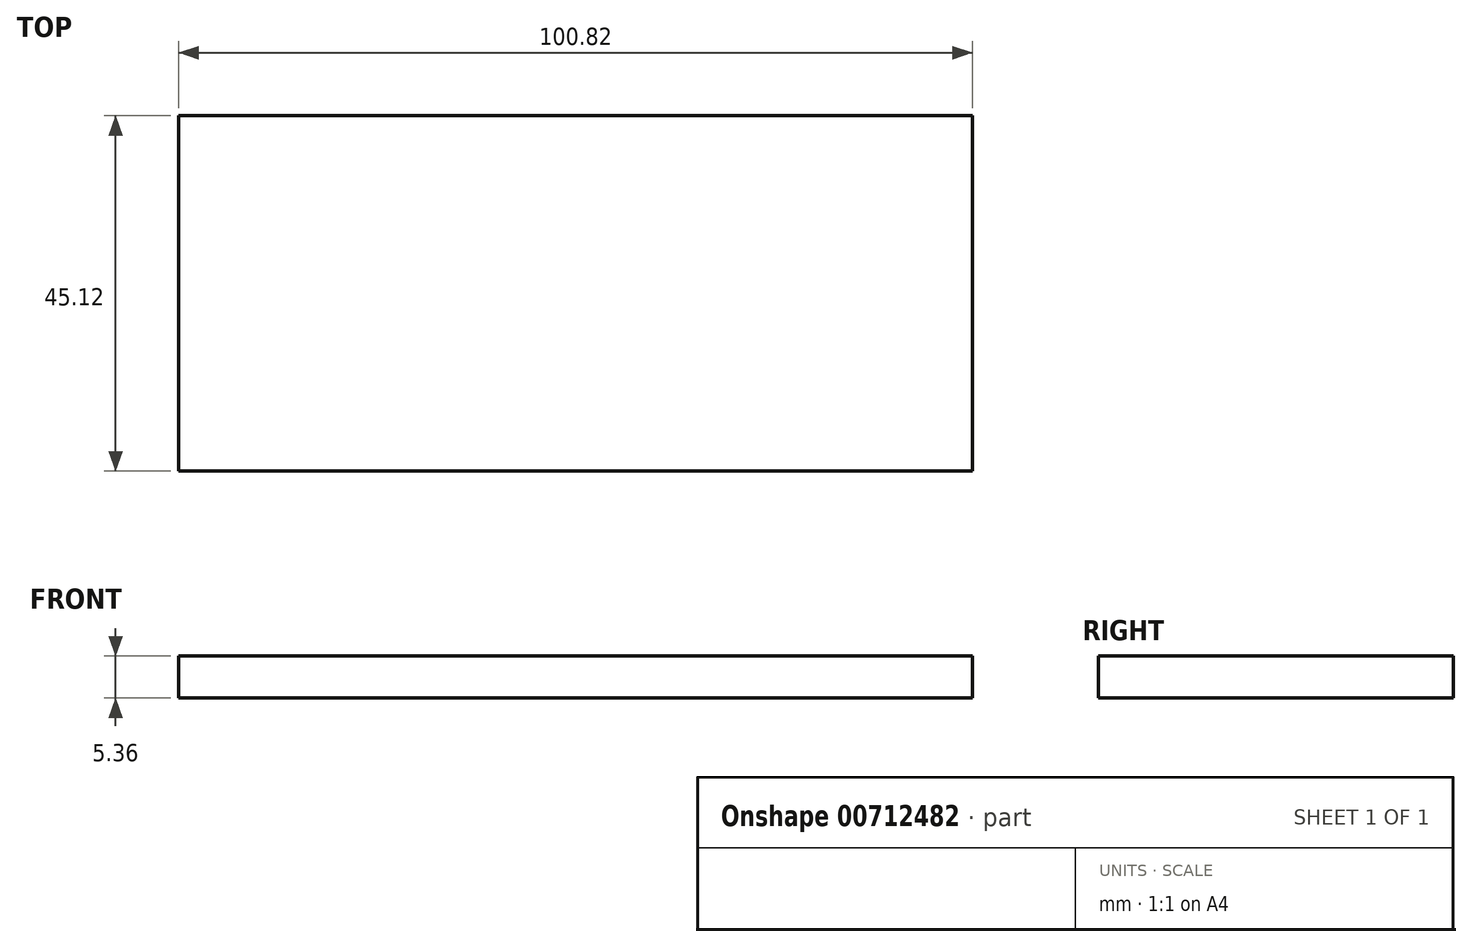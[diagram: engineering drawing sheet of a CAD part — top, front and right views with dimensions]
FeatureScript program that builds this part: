
annotation { "Feature Type Name" : "Feature", "Feature Type Description" : "" }
export const myFeature = defineFeature(function(context is Context, id is Id, definition is map)
    precondition{}
    {
        {
            var Q0;
            Q0=qCreatedBy(makeId("Top.planeOp"),FACE);
            var sketch = newSketch(context, id + "F0", { "sketchPlane" : qUnion([Q0])});
            skLineSegment(sketch, "E0.bottom", {"start": v(50.41, -22.56) * mm, "end": v(-50.41, -22.56) * mm});
            skLineSegment(sketch, "E0.top", {"start": v(50.41, 22.56) * mm, "end": v(-50.41, 22.56) * mm});
            skLineSegment(sketch, "E0.left", {"start": v(50.41, -22.56) * mm, "end": v(50.41, 22.56) * mm});
            skLineSegment(sketch, "E0.right", {"start": v(-50.41, -22.56) * mm, "end": v(-50.41, 22.56) * mm});
            skPoint(sketch, "E0.middle", {"position": v(0, 0) * mm});
            skSolve(sketch);
        }
        {
            var Q0;
            Q0=makeQuery(id+"F0.imprint","IMPRINT",FACE,{"disambiguationData":[TD([[makeQuery(id+"F0.imprint","IMPRINT",EDGE,{"derivedFrom":sQuery(id+"F0.wireOp",EDGE,"E0.bottom")}),-1.0]])]});
            extrude(context, id + "F1", {"entities" : qUnion([Q0]), "depth" : 5.36 * mm, "offsetDistance" : 25.4 * mm});
        }
    });
